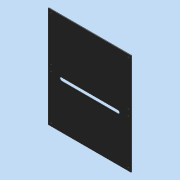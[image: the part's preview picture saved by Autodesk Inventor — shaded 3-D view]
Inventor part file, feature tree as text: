
AUTODESK INVENTOR PART (.ipt)
format: ipt  version: 2016 (Build 200138000, 138)  size: 112,640 bytes
history: native  units: mm
features: hole x8, extrude x2, sketch x2, fillet x1
ambient origin geometry x8: Origin, YZ Plane, XZ Plane, XY Plane, X Axis, Y Axis, Z Axis, Center Point
bodies: Solid1 (feature_tree)
feature tree (13):
  extrude  "Extrusion1"  Depth=440.0mm
  hole  "Hole1"  [1 undecoded]
  hole  "Hole2"  [1 undecoded]
  hole  "Hole3"  [1 undecoded]
  hole  "Hole4"  [1 undecoded]
  hole  "Hole5"  [1 undecoded]
  hole  "Hole6"  [1 undecoded]
  hole  "Hole7"  [1 undecoded]
  hole  "Hole8"  [1 undecoded]
  extrude  "Extrusion2"  Depth=3.0mm TaperAngle=0.0deg
  fillet  "Fillet1"  Radius=2.0mm
  sketch  "Sketch1"  dims[d0=360.0mm d1=440.0mm]
  sketch  "Sketch2"  dims[d2=3.0mm d3=0.0mm d4=12.0mm d5=12.0mm d6=4.0mm d7=6.0mm d8=4.0mm d9=2.0mm d10=90.0deg d11=8.0mm d12=20.594885mm d13=12.0mm d14=12.0mm d15=4.0mm d16=6.0mm d17=4.0mm d18=2.0mm d19=90.0deg d20=8.0mm d21=20.594885mm d22=12.0mm d23=12.0mm d24=4.0mm d25=6.0mm d26=4.0mm d27=2.0mm d28=90.0deg d29=8.0mm d30=20.594885mm d31=12.0mm d32=12.0mm d33=4.0mm d34=6.0mm d35=4.0mm d36=2.0mm d37=90.0deg d38=8.0mm d39=20.594885mm d40=12.0mm d41=206.5mm d42=4.0mm d43=6.0mm d44=4.0mm d45=2.0mm d46=90.0deg d47=8.0mm d48=20.594885mm d49=12.0mm d50=206.5mm d51=4.0mm d52=6.0mm d53=4.0mm d54=2.0mm d55=90.0deg d56=8.0mm d57=20.594885mm d58=12.0mm d59=206.5mm d60=4.0mm d61=6.0mm d62=4.0mm d63=2.0mm d64=90.0deg d65=8.0mm d66=20.594885mm d67=12.0mm d68=206.5mm d69=4.0mm d70=6.0mm d71=4.0mm d72=2.0mm d73=90.0deg d74=8.0mm d75=20.594885mm d76=3.0mm d77=0.0mm d78=2.0mm]
note: 8 required parameter values undecoded (feature->parameter linkage not recoverable at this tier; creation-order binding heuristic only, values carry confidence <= 0.55)
